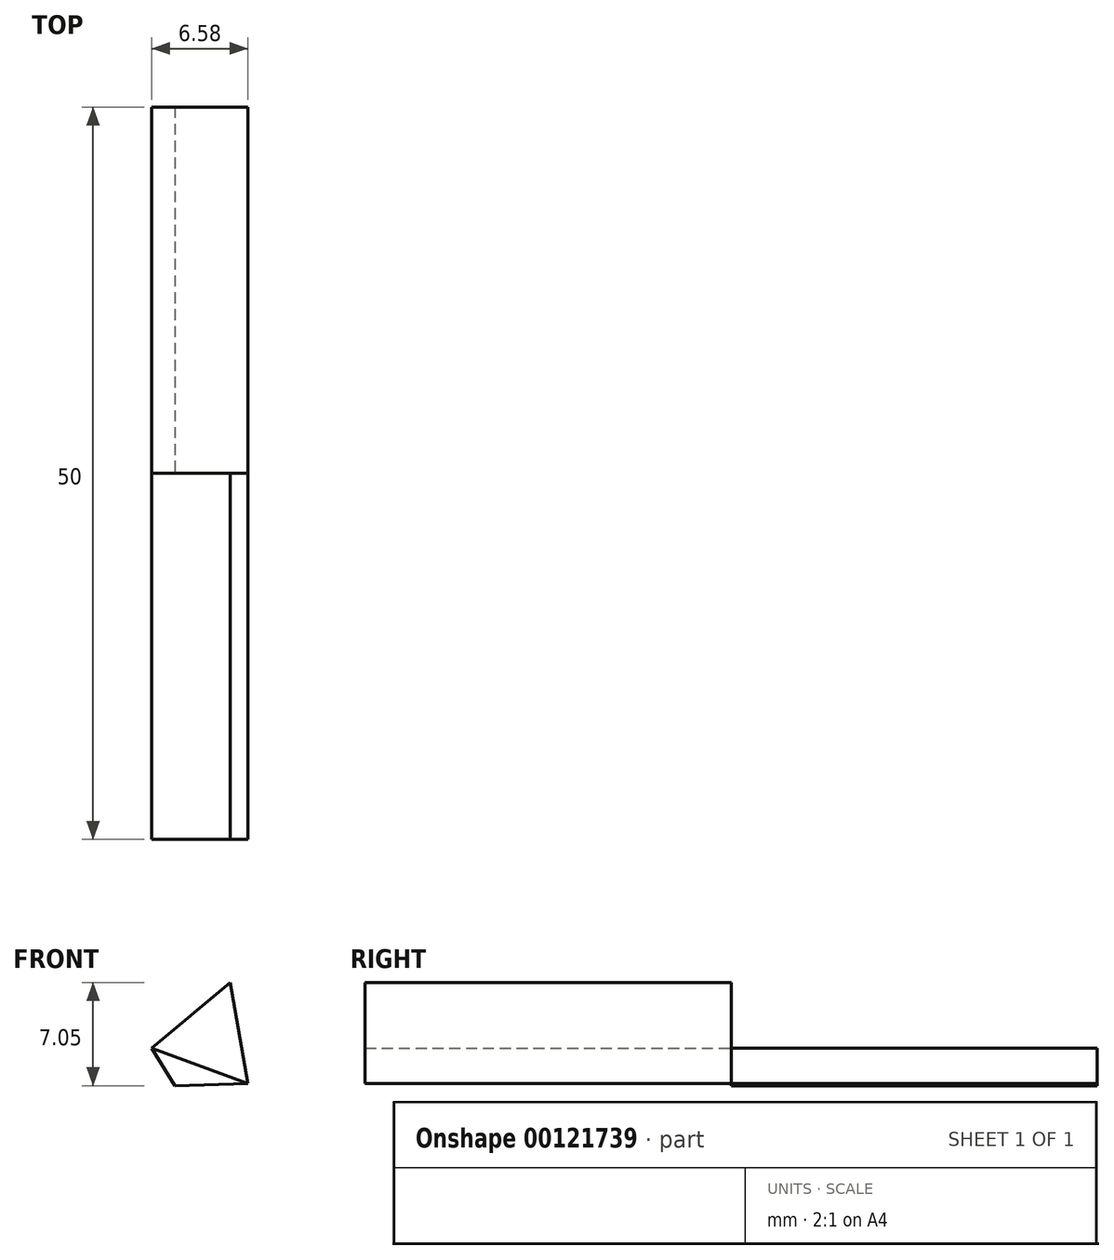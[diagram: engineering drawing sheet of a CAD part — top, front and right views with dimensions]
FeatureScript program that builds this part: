
annotation { "Feature Type Name" : "Feature", "Feature Type Description" : "" }
export const myFeature = defineFeature(function(context is Context, id is Id, definition is map)
    precondition{}
    {
        {
            var Q0;
            Q0=qCreatedBy(makeId("Front.planeOp"),FACE);
            var sketch = newSketch(context, id + "F0", { "sketchPlane" : qUnion([Q0])});
            skLineSegment(sketch, "E0", {"start": v(14.38, 19.95) * mm, "end": v(7.8, 22.34) * mm});
            skLineSegment(sketch, "E1", {"start": v(7.8, 22.34) * mm, "end": v(13.16, 26.84) * mm});
            skLineSegment(sketch, "E2", {"start": v(13.16, 26.84) * mm, "end": v(14.38, 19.95) * mm});
            skLineSegment(sketch, "E3", {"start": v(7.8, 22.34) * mm, "end": v(9.38, 19.79) * mm});
            skLineSegment(sketch, "E4", {"start": v(9.38, 19.79) * mm, "end": v(14.38, 19.95) * mm});
            skSolve(sketch);
        }
        {
            var Q0;
            Q0=makeQuery(id+"F0.imprint","IMPRINT",FACE,{"disambiguationData":[TD([[makeQuery(id+"F0.imprint","IMPRINT",EDGE,{"derivedFrom":sQuery(id+"F0.wireOp",EDGE,"E0")}),-1.0]])]});
            extrude(context, id + "F1", {"entities" : qUnion([Q0]), "depth" : 25 * mm});
        }
        {
            var Q0;
            Q0=makeQuery(id+"F0.imprint","IMPRINT",FACE,{"disambiguationData":[TD([[makeQuery(id+"F0.imprint","IMPRINT",EDGE,{"derivedFrom":sQuery(id+"F0.wireOp",EDGE,"E0")}),1.0]])]});
            extrude(context, id + "F2", {"entities" : qUnion([Q0]), "operationType" : NewBodyOperationType.ADD, "oppositeDirection" : true, "depth" : 25 * mm});
        }
    });
